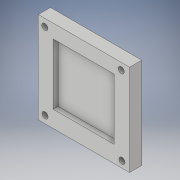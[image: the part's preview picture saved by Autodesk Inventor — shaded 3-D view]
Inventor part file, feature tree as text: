
AUTODESK INVENTOR PART (.ipt)
format: ipt  version: 2019 (Build 230136000, 136)  size: 108,544 bytes
history: native  units: mm
features: sketch x3, extrude x2, hole x1
ambient origin geometry x8: Origin, YZ Plane, XZ Plane, XY Plane, X Axis, Y Axis, Z Axis, Center Point
bodies: Solid1 (feature_tree)
feature tree (6):
  extrude  "Extrusion1"  Depth=150.0mm
  extrude  "Extrusion2"  Depth=100.0mm
  hole  "Hole1"  [1 undecoded]
  sketch  "Sketch1"  dims[d0=150.0mm d1=150.0mm]
  sketch  "Sketch2"  dims[d2=20.0mm d3=0.0mm d4=100.0mm]
  sketch  "Sketch3"  dims[d5=100.0mm d6=8.0mm d7=0.0mm d8=10.0mm d9=6.0mm d10=4.0mm d11=2.0mm d12=90.0deg d13=30.0mm d14=20.594885mm]
note: 1 required parameter value undecoded (feature->parameter linkage not recoverable at this tier; creation-order binding heuristic only, values carry confidence <= 0.55)
